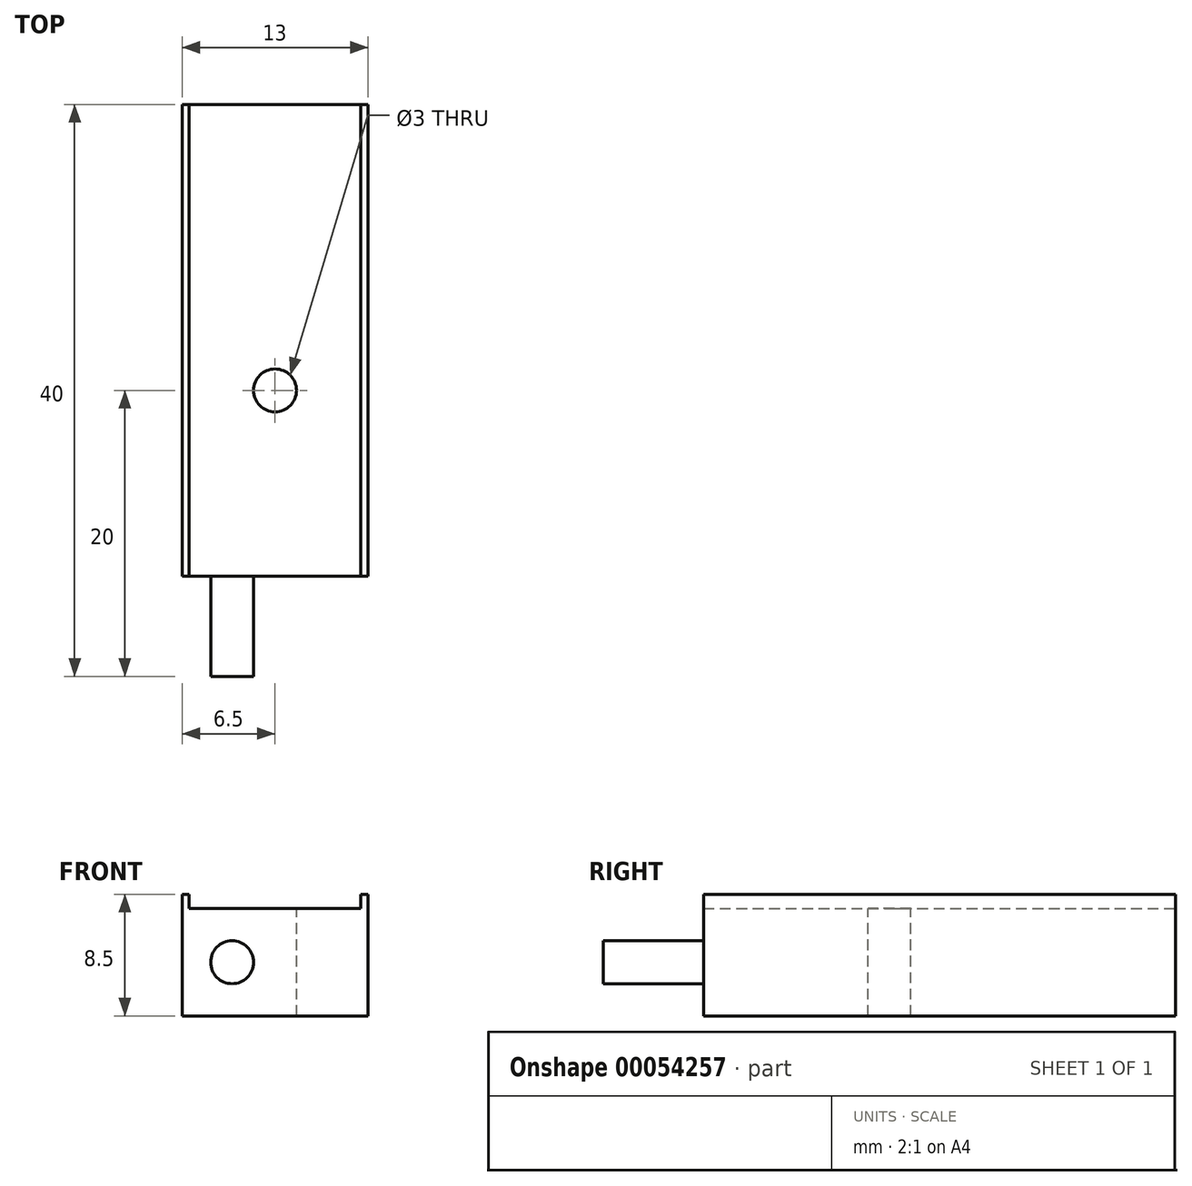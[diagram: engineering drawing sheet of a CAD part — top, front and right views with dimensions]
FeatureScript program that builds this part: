
annotation { "Feature Type Name" : "Feature", "Feature Type Description" : "" }
export const myFeature = defineFeature(function(context is Context, id is Id, definition is map)
    precondition{}
    {
        {
            var Q0;
            Q0=qCreatedBy(makeId("Front.planeOp"),FACE);
            var sketch = newSketch(context, id + "F0", { "sketchPlane" : qUnion([Q0])});
            skLineSegment(sketch, "E0", {"start": v(0, 35.44) * mm, "end": v(0, -40.22) * mm, "construction": true});
            skLineSegment(sketch, "E1.0", {"start": v(-6.5, 8.5) * mm, "end": v(-6.5, 0) * mm, "construction": true});
            skLineSegment(sketch, "E2", {"start": v(0, 0) * mm, "end": v(-6.5, 0) * mm, "construction": true});
            skLineSegment(sketch, "E3.0", {"start": v(0, 8.5) * mm, "end": v(-6.5, 8.5) * mm, "construction": true});
            skLineSegment(sketch, "E4.0", {"start": v(-6, 8.5) * mm, "end": v(-6, 0) * mm, "construction": true});
            skLineSegment(sketch, "E5.0", {"start": v(0, 7.5) * mm, "end": v(-6.5, 7.5) * mm, "construction": true});
            skLineSegment(sketch, "E6", {"start": v(0, 7.5) * mm, "end": v(-6, 7.5) * mm});
            skLineSegment(sketch, "E7", {"start": v(-6, 7.5) * mm, "end": v(-6, 8.5) * mm});
            skLineSegment(sketch, "E8", {"start": v(-6.5, 8.5) * mm, "end": v(-6.5, 0) * mm});
            skLineSegment(sketch, "E9", {"start": v(0, 0) * mm, "end": v(-6.5, 0) * mm});
            skLineSegment(sketch, "E10", {"start": v(-6.5, 8.5) * mm, "end": v(-6, 8.5) * mm});
            skLineSegment(sketch, "E11", {"start": v(0, 7.5) * mm, "end": v(0, 0) * mm});
            skLineSegment(sketch, "E12.MirrorCS", {"start": v(0, 7.5) * mm, "end": v(6, 7.5) * mm});
            skLineSegment(sketch, "E13.MirrorCS", {"start": v(6, 7.5) * mm, "end": v(6, 8.5) * mm});
            skLineSegment(sketch, "E14.MirrorCS", {"start": v(6.5, 8.5) * mm, "end": v(6, 8.5) * mm});
            skLineSegment(sketch, "E15.MirrorCS", {"start": v(6.5, 8.5) * mm, "end": v(6.5, 0) * mm});
            skLineSegment(sketch, "E16.MirrorCS", {"start": v(0, 0) * mm, "end": v(6.5, 0) * mm});
            skSolve(sketch);
        }
        {
            var Q0;
            Q0=makeQuery(id+"F0.imprint","IMPRINT",FACE,{"disambiguationData":[TD([[makeQuery(id+"F0.imprint","IMPRINT",EDGE,{"derivedFrom":sQuery(id+"F0.wireOp",EDGE,"E6")}),1.0]])]});
            var Q1;
            Q1=makeQuery(id+"F0.imprint","IMPRINT",FACE,{"disambiguationData":[TD([[makeQuery(id+"F0.imprint","IMPRINT",EDGE,{"derivedFrom":sQuery(id+"F0.wireOp",EDGE,"E11")}),1.0]])]});
            extrude(context, id + "F1", {"entities" : qUnion([Q0, Q1]), "depth" : 40 * mm});
        }
        {
            var Q0;
            Q0=makeQuery(id+"F1.opExtrude","SWEPT_FACE",FACE,{"disambiguationData":[OSD([sQuery(id+"F0.wireOp",EDGE,"E6"),sQuery(id+"F0.wireOp",EDGE,"E12.MirrorCS")])]});
            var sketch = newSketch(context, id + "F2", { "sketchPlane" : qUnion([Q0])});
            skLineSegment(sketch, "E17.0.0", {"start": v(6, 0) * mm, "end": v(-6, 0) * mm, "construction": true});
            skLineSegment(sketch, "E17.0.1", {"start": v(-6, 0) * mm, "end": v(-6, -40) * mm});
            skLineSegment(sketch, "E17.0.2", {"start": v(-6, -40) * mm, "end": v(6, -40) * mm});
            skLineSegment(sketch, "E17.0.3", {"start": v(6, -40) * mm, "end": v(6, 0) * mm});
            skLineSegment(sketch, "E18", {"start": v(0, 0) * mm, "end": v(0, -40) * mm, "construction": true});
            skCircle(sketch, "E19", {"center": v(0, -20) * mm, "radius": 1.5 * mm});
            skSolve(sketch);
        }
        {
            var Q0;
            Q0=makeQuery(id+"F2.imprint","IMPRINT",FACE,{"disambiguationData":[TD([[makeQuery(id+"F2.imprint","IMPRINT",EDGE,{"derivedFrom":sQuery(id+"F2.wireOp",EDGE,"E19")}),1.0]])]});
            extrude(context, id + "F3", {"entities" : qUnion([Q0]), "operationType" : NewBodyOperationType.REMOVE, "oppositeDirection" : true, "depth" : 25 * mm});
        }
        {
            var Q0;
            Q0=makeQuery(id+"F1.opExtrude","CAP_FACE",FACE,{"disambiguationData":[OSD([sQuery(id+"F0.wireOp",EDGE,"E6"),sQuery(id+"F0.wireOp",EDGE,"E7"),sQuery(id+"F0.wireOp",EDGE,"E8"),sQuery(id+"F0.wireOp",EDGE,"E9"),sQuery(id+"F0.wireOp",EDGE,"E10"),sQuery(id+"F0.wireOp",EDGE,"E12.MirrorCS"),sQuery(id+"F0.wireOp",EDGE,"E13.MirrorCS"),sQuery(id+"F0.wireOp",EDGE,"E14.MirrorCS"),sQuery(id+"F0.wireOp",EDGE,"E15.MirrorCS"),sQuery(id+"F0.wireOp",EDGE,"E16.MirrorCS")])],"isStart":false});
            var sketch = newSketch(context, id + "F4", { "sketchPlane" : qUnion([Q0])});
            skLineSegment(sketch, "E20.0.0", {"start": v(-6.5, 0) * mm, "end": v(6.5, 0) * mm});
            skLineSegment(sketch, "E20.0.1", {"start": v(6.5, 0) * mm, "end": v(6.5, 8.5) * mm});
            skLineSegment(sketch, "E20.0.2", {"start": v(6.5, 8.5) * mm, "end": v(6, 8.5) * mm});
            skLineSegment(sketch, "E20.0.3", {"start": v(6, 8.5) * mm, "end": v(6, 7.5) * mm});
            skLineSegment(sketch, "E20.0.4", {"start": v(6, 7.5) * mm, "end": v(-6, 7.5) * mm});
            skLineSegment(sketch, "E20.0.5", {"start": v(-6, 7.5) * mm, "end": v(-6, 8.5) * mm});
            skLineSegment(sketch, "E20.0.6", {"start": v(-6, 8.5) * mm, "end": v(-6.5, 8.5) * mm});
            skLineSegment(sketch, "E20.0.7", {"start": v(-6.5, 8.5) * mm, "end": v(-6.5, 0) * mm});
            skLineSegment(sketch, "E21", {"start": v(0, 7.5) * mm, "end": v(0, 0) * mm, "construction": true});
            skLineSegment(sketch, "E22", {"start": v(6, 7.5) * mm, "end": v(6, 0) * mm, "construction": true});
            skLineSegment(sketch, "E23", {"start": v(6, 3.75) * mm, "end": v(0, 3.75) * mm, "construction": true});
            skCircle(sketch, "E24", {"center": v(3, 3.75) * mm, "radius": 1.5 * mm});
            skCircle(sketch, "E25.MirrorC", {"center": v(-3, 3.75) * mm, "radius": 1.5 * mm});
            skSolve(sketch);
        }
        {
            var Q0;
            Q0=makeQuery(id+"F4.imprint","IMPRINT",FACE,{"disambiguationData":[TD([[makeQuery(id+"F4.imprint","IMPRINT",EDGE,{"derivedFrom":sQuery(id+"F4.wireOp",EDGE,"E25.MirrorC")}),-1.0]])]});
            var Q1;
            Q1=makeQuery(id+"F4.imprint","IMPRINT",FACE,{"disambiguationData":[TD([[makeQuery(id+"F4.imprint","IMPRINT",EDGE,{"derivedFrom":sQuery(id+"F4.wireOp",EDGE,"E24")}),1.0]])]});
            extrude(context, id + "F5", {"entities" : qUnion([Q0, Q1]), "operationType" : NewBodyOperationType.REMOVE, "oppositeDirection" : true, "depth" : 7 * mm});
        }
    });
